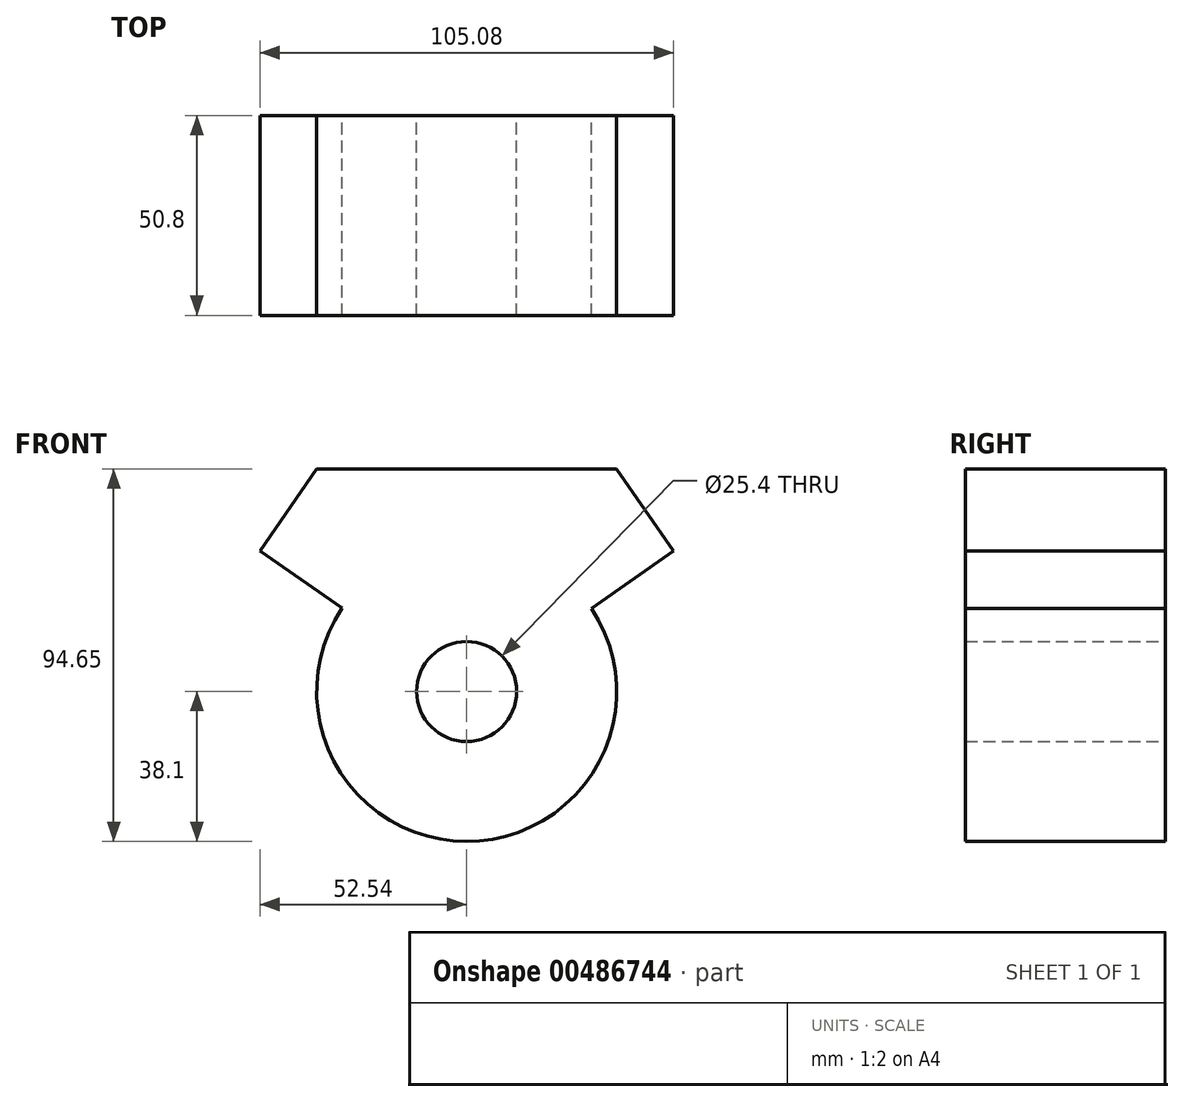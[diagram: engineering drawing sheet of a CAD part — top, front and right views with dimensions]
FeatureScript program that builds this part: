
annotation { "Feature Type Name" : "Feature", "Feature Type Description" : "" }
export const myFeature = defineFeature(function(context is Context, id is Id, definition is map)
    precondition{}
    {
        {
            var Q0;
            Q0=qCreatedBy(makeId("Front.planeOp"),FACE);
            var sketch = newSketch(context, id + "F0", { "sketchPlane" : qUnion([Q0])});
            skArc(sketch, "E0", {"start": v(-31.61, 21.27) * mm, "mid": v(-0.1, -38.1) * mm, "end": v(31.73, 21.09) * mm});
            skCircle(sketch, "E1", {"center": v(0, 0) * mm, "radius": 12.7 * mm});
            skLineSegment(sketch, "E2", {"start": v(-52.54, 35.66) * mm, "end": v(-38.1, 56.55) * mm});
            skLineSegment(sketch, "E3", {"start": v(-38.1, 56.55) * mm, "end": v(38.1, 56.55) * mm});
            skLineSegment(sketch, "E4", {"start": v(38.1, 56.55) * mm, "end": v(52.54, 35.66) * mm});
            skLineSegment(sketch, "E5", {"start": v(52.54, 35.66) * mm, "end": v(31.73, 21.09) * mm});
            skLineSegment(sketch, "E6.trimOffspring", {"start": v(-31.61, 21.27) * mm, "end": v(-52.54, 35.66) * mm});
            skSolve(sketch);
        }
        {
            var Q0;
            Q0=makeQuery(id+"F0.imprint","IMPRINT",FACE,{"disambiguationData":[TD([[makeQuery(id+"F0.imprint","IMPRINT",EDGE,{"derivedFrom":sQuery(id+"F0.wireOp",EDGE,"E0")}),1.0]])]});
            extrude(context, id + "F1", {"entities" : qUnion([Q0]), "depth" : 50.8 * mm});
        }
    });
